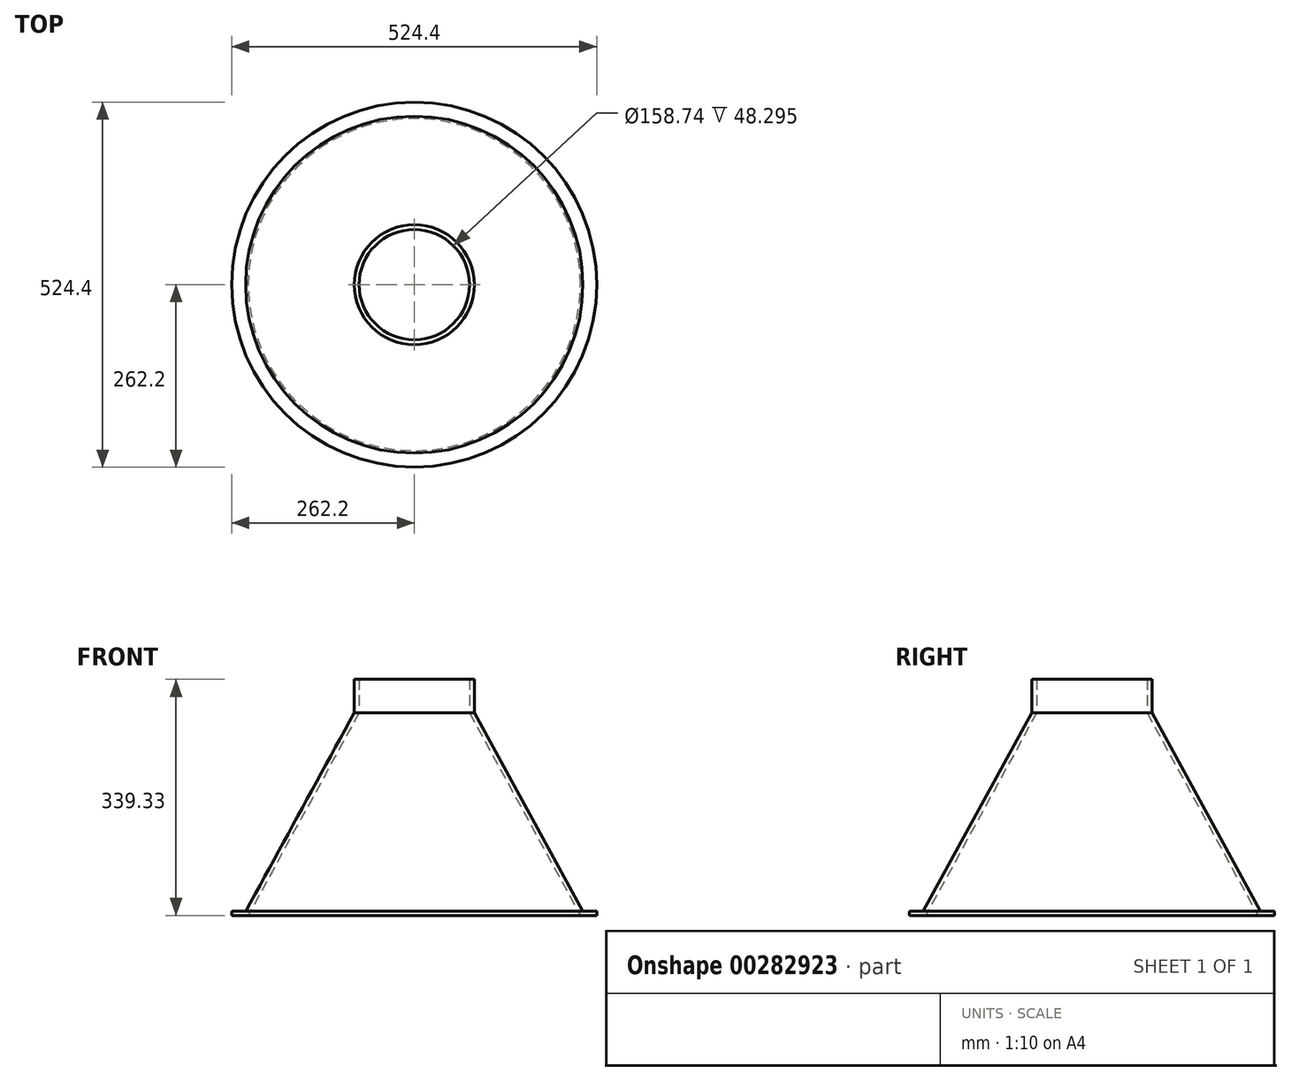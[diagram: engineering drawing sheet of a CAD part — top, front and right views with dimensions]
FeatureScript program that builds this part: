
annotation { "Feature Type Name" : "Feature", "Feature Type Description" : "" }
export const myFeature = defineFeature(function(context is Context, id is Id, definition is map)
    precondition{}
    {
        {
            var Q0;
            Q0=qCreatedBy(makeId("Front.planeOp"),FACE);
            var sketch = newSketch(context, id + "F0", { "sketchPlane" : qUnion([Q0])});
            skLineSegment(sketch, "E0", {"start": v(-262.2, 0) * mm, "end": v(-262.2, 6) * mm});
            skLineSegment(sketch, "E1", {"start": v(-262.2, 6) * mm, "end": v(-242.2, 6) * mm});
            skLineSegment(sketch, "E2", {"start": v(-262.2, 0) * mm, "end": v(-238.64, 0) * mm});
            skLineSegment(sketch, "E3", {"start": v(0, 0) * mm, "end": v(0, 304) * mm, "construction": true});
            skPoint(sketch, "E4.visualSharp", {"position": v(-242.2, 6) * mm});
            skLineSegment(sketch, "E5", {"start": v(-242.2, 6) * mm, "end": v(-86.21, 291.04) * mm});
            skLineSegment(sketch, "E6.0", {"start": v(-238.64, 0) * mm, "end": v(-79.37, 291.04) * mm});
            skLineSegment(sketch, "E7", {"start": v(-86.21, 291.04) * mm, "end": v(-86.21, 339.33) * mm});
            skLineSegment(sketch, "E8", {"start": v(-86.21, 339.33) * mm, "end": v(-79.37, 339.33) * mm});
            skLineSegment(sketch, "E9", {"start": v(-79.37, 339.33) * mm, "end": v(-79.37, 291.04) * mm});
            skSolve(sketch);
        }
        {
            var Q0;
            Q0 = qSketchRegion(id + "F0", true);
            var Q1;
            Q1=sQuery(id+"F0.wireOp",EDGE,"E3");
            revolve(context, id + "F1", {"entities" : qUnion([Q0]), "axis" : qUnion([Q1]), "revolveType" : RevolveType.FULL});
        }
    });
